# Revit family: BISLEY_SystemFile_Lodges
name_source: partatom
category: Furniture
revit_build: Autodesk Revit 2018 (Build: 20180423_1000(x64)
units: mm (PartAtom-declared; Revit-internal decimal feet)

## family parameters
Always vertical = Yes
Cut with Voids When Loaded = No
OmniClass Number = 23.40.20.00
OmniClass Title = General Furniture and Specialties
Room Calculation Point = No
Shared = No
Work Plane-Based = No

## types (15) — shared parameters
Category = Furniture
Compliance Standards Certification = BS EN 14073 2004 Part 2 & 3, BS EN 14074, BS 4875 1998 Part 7 level 4 & Part 8, BS 476 Part 7 1987 Class 2Y
Depth = 470 mm
Finish = Powder Coated
LockerType = Systemfile
Manufacturer = Bisley
Material = Steel
Model = Systemfile Lodge
Name = Systemfile Lodge
Routine Maintenance = We recommend you clean your unit with warm water and a mild detergent solution. A damp cloth can be used to remove dust particles.
Uniclass 2015 Code = PR_40_30_57
Uniclass2015Title = Shelves and Storage Units
Uniclass2015Version = V1.1
Warranty = 10 years

## per-type parameters (varying)
| type | 1st Row DOUBLE | 1st Row Doors Height | 1st Row TRIPLE | 2nd Row DOUBLE | 2nd Row Doors Height | 2nd Row TRIPLE | 3rd Row DOUBLE | 3rd Row Doors Height | 3rd Row TRIPLE | 4th Row DOUBLE | 4th Row Doors Height | 4th Row TRIPLE | 4th Row Tie Bar | 5th Row DOUBLE | 5th Row Door Height | 5th Row TRIPLE | 5th Row Tie Bar | Colour | Height | Model Reference | Product Information | URL | Width |
| SYL0830LS2JA | Yes | 303 mm | No | Yes | 262 mm | No | Yes | 262 mm | No | No | 305 mm | No | No | No | 305 mm | No | No |  | 997 mm | SYL0830LS2JA | 2 pairs of 266.7mm doors and 1 pair of 304.8mm doors | www.bisley.com | 800 mm  [stored 2.62467 ft] |
| SYL1030LS2JA | Yes | 303 mm | No | Yes | 262 mm | No | Yes | 262 mm | No | No | 305 mm | No | No | No | 305 mm | No | No |  | 997 mm | SYL1030LS2JA | 2 pairs of 266.7mm and 1 pair of 304.8mm doors | www.bisley.com | 1000 mm  [stored 3.28084 ft] |
| SYL0834LSA2B | Yes | 337 mm | No | Yes | 337 mm | No | Yes | 303 mm | No | No | 305 mm | No | No | No | 305 mm | No | No |  | 1149 mm | SYL0834LSA2B | 1 pair of 304.88 doors and 2 pairs of 342.9mm doors. | www.bisley.com | 800 mm  [stored 2.62467 ft] |
| SYL1034LSA2B | Yes | 337 mm | No | Yes | 337 mm | No | Yes | 303 mm | No | No | 305 mm | No | No | No | 305 mm | No | No |  | 1149 mm | SYL1034LSA2B | 1 x pair of 304.8mm and 2 x pair of 342.9 doors | www.bisley.com | 1000 mm  [stored 3.28084 ft] |
| SYL0840LS3JA | Yes | 303 mm | No | Yes | 262 mm | No | Yes | 262 mm | No | Yes | 262 mm | No | Yes | No | 305 mm | No | No |  | 1301 mm | SYL0840LS3JA | 3 pairs of 266.7mm doors and 1 pair of 304.8mm doors | www.bisley.com | 800 mm  [stored 2.62467 ft] |
| SYL1040LS3JA | Yes | 303 mm | No | Yes | 262 mm | No | Yes | 262 mm | No | Yes | 262 mm | No | Yes | No | 305 mm | No | No |  | 1301 mm | SYL1040LS3JA | 3 x pais of 266.7mm and 1 x pair of 304.8mm doors | www.bisley.com | 1000 mm  [stored 3.28084 ft] |
| SYL0850LS3J2A | Yes | 303 mm | No | Yes | 303 mm | No | Yes | 262 mm | No | Yes | 262 mm | No | Yes | Yes | 262 mm | No | Yes |  | 1643 mm | SYL0850LS3J2A | 3 pairs of 266.7mm doors and 2 pair of 304.8mm doors | www.bisley.com | 800 mm  [stored 2.62467 ft] |
| SYL1050LS3J2A | Yes | 303 mm | No | Yes | 303 mm | No | Yes | 262 mm | No | Yes | 262 mm | No | Yes | Yes | 262 mm | No | Yes |  | 1643 mm | SYL1050LS3J2A | 3 x pairs of 266.7mm and 2 x pairs of 304.8mm doors | www.bisley.com | 1000 mm  [stored 3.28084 ft] |
| SYL0860LS5B | Yes | 338 mm | No | Yes | 338 mm | No | Yes | 338 mm | No | Yes | 338 mm | No | Yes | Yes | 338 mm | No | Yes |  | 1947 mm | SYL0850LS3J2A | 5 x pairs of 342.9mm doors | www.bisley.com | 800 mm  [stored 2.62467 ft] |
| SYL1060LS5B | Yes | 338 mm | No | Yes | 338 mm | No | Yes | 338 mm | No | Yes | 338 mm | No | Yes | Yes | 338 mm | No | Yes | BS EN 14073-2: 2004, BS EN 14073-3: 2004, BS EN 14074: 2004 | 1947 mm | SYL1060LS5B | 5 x pairs of 342.9mm doors | www.bisley.com | 1000 mm  [stored 3.28084 ft] |
| SYL1060LT5B | No | 338 mm | Yes | No | 338 mm | Yes | No | 338 mm | Yes | No | 338 mm | Yes | Yes | No | 338 mm | Yes | Yes |  | 1947 mm | SYL1060LT5B | 15 x 342.9mm doors | www.bisley.com | 1000 mm  [stored 3.28084 ft] |
| SYL1050LT3J2A | No | 302 mm | Yes | No | 302 mm | Yes | No | 261 mm | Yes | No | 261 mm | Yes | Yes | No | 261 mm | Yes | Yes |  | 1643 mm | SYL1050LT3J2A | 9 x 266.7mm and 6 x 304.8mm doors |  | 1000 mm  [stored 3.28084 ft] |
| SYL1040LT3JA | No | 303 mm | Yes | No | 261 mm | Yes | No | 261 mm | Yes | No | 261 mm | Yes | Yes | No | 261 mm | No | No |  | 1301 mm | SYL1040LT3JA | 9 X 266.7mm and 2 x 304.8mm doors | www.bisley.com | 1000 mm  [stored 3.28084 ft] |
| SYL1034LTA2B | No | 337 mm | Yes | No | 337 mm | Yes | No | 303 mm | Yes | No | 261 mm | No | No | No | 261 mm | No | No |  | 1149 mm | SYL1034LTA2B | 3 x 304.8mm doors and 6 x 342.9mm doors | www.bisley.com | 1000 mm  [stored 3.28084 ft] |
| SYL1030LT2JA | No | 303 mm | Yes | No | 262 mm | Yes | No | 262 mm | Yes | No | 261 mm | No | No | No | 261 mm | No | No |  | 997 mm | SYL1030LT2JA | 6 x 266.7mm doors and 3 x 304.8mm doors | www.bisley.com | 1000 mm  [stored 3.28084 ft] |

note: [stored X ft] marks values corroborated as IEEE doubles in the binary element streams (Revit-internal decimal feet)

## geometry (parser evidence)
native form markers: Sweep x3
no freeform markers — native parametric forms only
